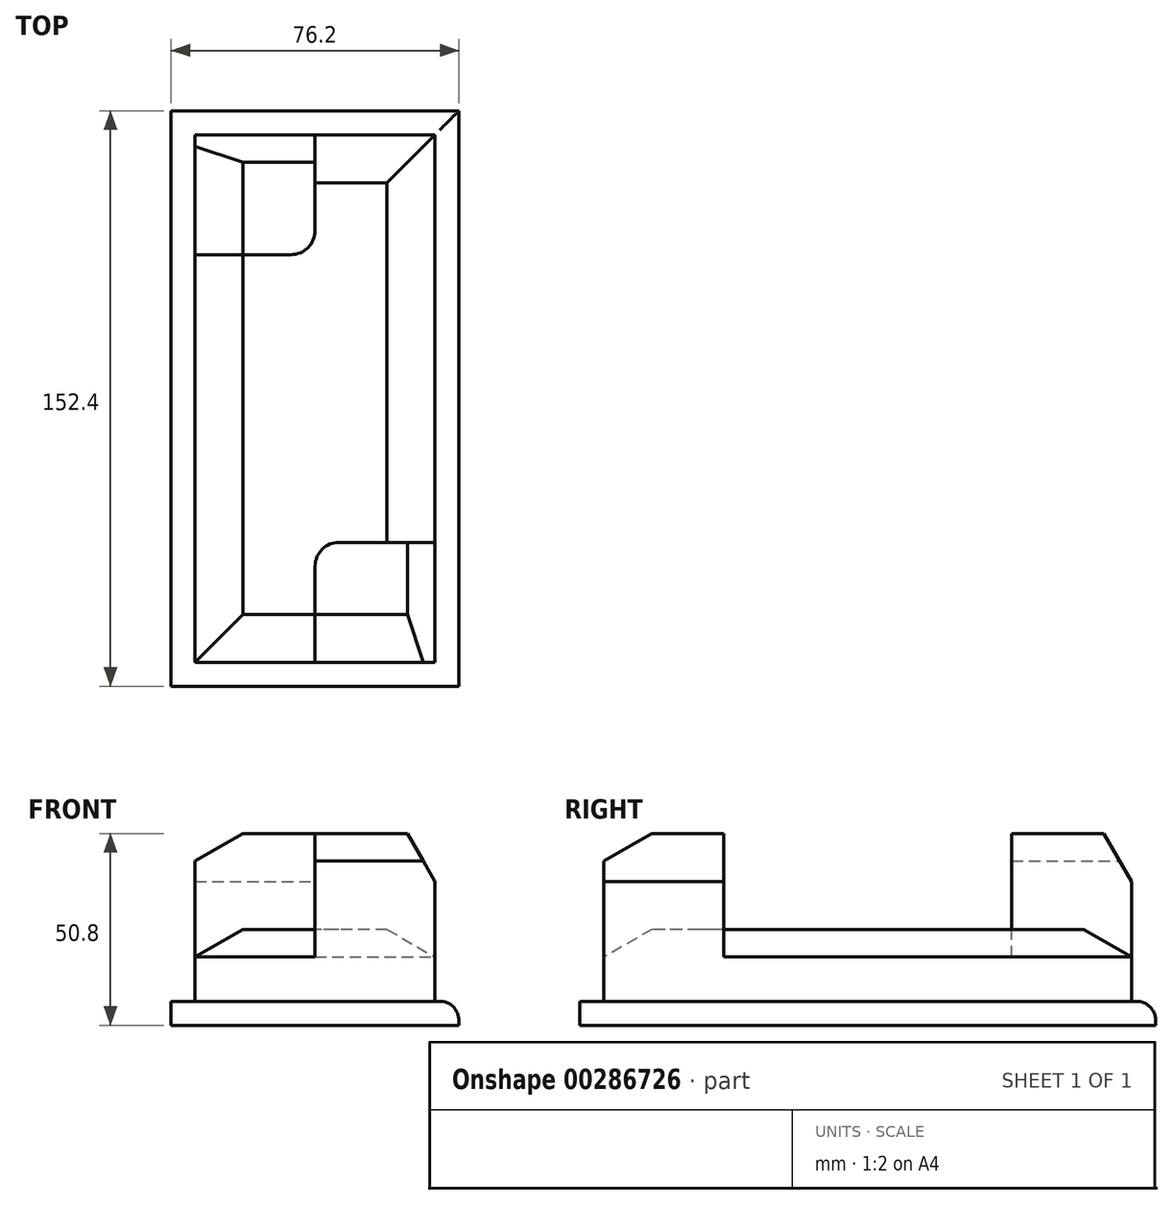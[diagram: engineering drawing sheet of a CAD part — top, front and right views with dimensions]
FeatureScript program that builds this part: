
annotation { "Feature Type Name" : "Feature", "Feature Type Description" : "" }
export const myFeature = defineFeature(function(context is Context, id is Id, definition is map)
    precondition{}
    {
        {
            var Q0;
            Q0=qCreatedBy(makeId("Top.planeOp"),FACE);
            var sketch = newSketch(context, id + "F0", { "sketchPlane" : qUnion([Q0])});
            skLineSegment(sketch, "E0.bottom", {"start": v(-35.8, 87.47) * mm, "end": v(40.4, 87.47) * mm});
            skLineSegment(sketch, "E0.top", {"start": v(-35.8, -64.93) * mm, "end": v(40.4, -64.93) * mm});
            skLineSegment(sketch, "E0.left", {"start": v(-35.8, 87.47) * mm, "end": v(-35.8, -64.93) * mm});
            skLineSegment(sketch, "E0.right", {"start": v(40.4, 87.47) * mm, "end": v(40.4, -64.93) * mm});
            skLineSegment(sketch, "E1.bottom", {"start": v(-29.45, 81.12) * mm, "end": v(34.05, 81.12) * mm});
            skLineSegment(sketch, "E1.top", {"start": v(-29.45, -58.58) * mm, "end": v(34.05, -58.58) * mm});
            skLineSegment(sketch, "E1.left", {"start": v(-29.45, 81.12) * mm, "end": v(-29.45, -58.58) * mm});
            skLineSegment(sketch, "E1.right", {"start": v(34.05, 81.12) * mm, "end": v(34.05, -58.58) * mm});
            skLineSegment(sketch, "E2", {"start": v(-29.45, 49.37) * mm, "end": v(2.3, 49.37) * mm});
            skLineSegment(sketch, "E3", {"start": v(2.3, 49.37) * mm, "end": v(2.3, 81.12) * mm});
            skPoint(sketch, "E3.endSnap0", {"position": v(2.3, 81.12) * mm});
            skLineSegment(sketch, "E4", {"start": v(34.05, -26.83) * mm, "end": v(2.3, -26.83) * mm});
            skLineSegment(sketch, "E5", {"start": v(2.3, -26.83) * mm, "end": v(2.3, -58.58) * mm});
            skSolve(sketch);
        }
        {
            var Q0;
            Q0=makeQuery(id+"F0.imprint","IMPRINT",FACE,{"disambiguationData":[TD([[makeQuery(id+"F0.imprint","IMPRINT",EDGE,{"derivedFrom":sQuery(id+"F0.wireOp",EDGE,"E0.bottom")}),-1.0]])]});
            extrude(context, id + "F1", {"entities" : qUnion([Q0]), "depth" : 6.35 * mm});
        }
        {
            var Q0;
            {var subQ3=sQuery(id+"F0.wireOp",EDGE,"E2");Q0=makeQuery(id+"F0.imprint","IMPRINT",FACE,{"disambiguationData":[TD([[makeQuery(id+"F0.imprint","IMPRINT",EDGE,{"derivedFrom":subQ3}),-1.0]])]});}
            extrude(context, id + "F2", {"entities" : qUnion([Q0]), "operationType" : NewBodyOperationType.ADD, "depth" : 25.4 * mm});
        }
        {
            var Q0;
            {var subQ4=sQuery(id+"F0.wireOp",EDGE,"E2");Q0=makeQuery(id+"F0.imprint","IMPRINT",FACE,{"disambiguationData":[TD([[makeQuery(id+"F0.imprint","IMPRINT",EDGE,{"derivedFrom":subQ4}),1.0]])]});}
            var Q1;
            {var subQ4=sQuery(id+"F0.wireOp",EDGE,"E4");Q1=makeQuery(id+"F0.imprint","IMPRINT",FACE,{"disambiguationData":[TD([[makeQuery(id+"F0.imprint","IMPRINT",EDGE,{"derivedFrom":subQ4}),1.0]])]});}
            extrude(context, id + "F3", {"entities" : qUnion([Q0, Q1]), "operationType" : NewBodyOperationType.ADD, "depth" : 50.8 * mm});
        }
        {
            var Q0;
            Q0=makeQuery(id+"F2.opExtrude","CAP_EDGE",EDGE,{"disambiguationData":[OSD([sQuery(id+"F0.wireOp",EDGE,"E1.left")])],"isStart":false});
            var Q1;
            Q1=makeQuery(id+"F2.opExtrude","CAP_EDGE",EDGE,{"disambiguationData":[OSD([sQuery(id+"F0.wireOp",EDGE,"E1.top")])],"isStart":false});
            var Q2;
            Q2=makeQuery(id+"F3.opExtrude","CAP_EDGE",EDGE,{"disambiguationData":[OSD([sQuery(id+"F0.wireOp",EDGE,"E1.top")])],"isStart":false});
            var Q3;
            Q3=makeQuery(id+"F3.opExtrude","CAP_EDGE",EDGE,{"disambiguationData":[OSD([sQuery(id+"F0.wireOp",EDGE,"E1.left")])],"isStart":false});
            var Q4;
            Q4=makeQuery(id+"F3.opExtrude","CAP_EDGE",EDGE,{"disambiguationData":[OSD([sQuery(id+"F0.wireOp",EDGE,"E1.right")])],"isStart":false});
            var Q5;
            Q5=makeQuery(id+"F2.opExtrude","CAP_EDGE",EDGE,{"disambiguationData":[OSD([sQuery(id+"F0.wireOp",EDGE,"E1.right")])],"isStart":false});
            var Q6;
            Q6=makeQuery(id+"F2.opExtrude","CAP_EDGE",EDGE,{"disambiguationData":[OSD([sQuery(id+"F0.wireOp",EDGE,"E1.bottom")])],"isStart":false});
            var Q7;
            Q7=makeQuery(id+"F3.opExtrude","CAP_EDGE",EDGE,{"disambiguationData":[OSD([sQuery(id+"F0.wireOp",EDGE,"E1.bottom")])],"isStart":false});
            chamfer(context, id + "F4", {"entities" : qUnion([Q0, Q1, Q2, Q3, Q4, Q5, Q6, Q7]), "chamferType" : ChamferType.OFFSET_ANGLE, "width" : 12.7 * mm, "oppositeDirection" : false, "angle" : 30 * degree, "tangentPropagation" : true});
        }
        {
            var Q0;
            Q0=makeQuery(id+"F3.opExtrude","SWEPT_EDGE",EDGE,{"disambiguationData":[OSD([sQuery(id+"F0.wireOp",EDGE,"E2"),sQuery(id+"F0.wireOp",EDGE,"E3")])]});
            var Q1;
            Q1=makeQuery(id+"F3.opExtrude","SWEPT_EDGE",EDGE,{"disambiguationData":[OSD([sQuery(id+"F0.wireOp",EDGE,"E4"),sQuery(id+"F0.wireOp",EDGE,"E5")])]});
            fillet(context, id + "F5", {"entities" : qUnion([Q0, Q1]), "radius" : 6.35 * mm, "tangentPropagation" : true, "allowEdgeOverflow" : false});
        }
        {
            var Q0;
            Q0=makeQuery(id+"F1.opExtrude","CAP_EDGE",EDGE,{"disambiguationData":[OSD([sQuery(id+"F0.wireOp",EDGE,"E0.bottom")])],"isStart":false});
            var Q1;
            Q1=makeQuery(id+"F1.opExtrude","CAP_EDGE",EDGE,{"disambiguationData":[OSD([sQuery(id+"F0.wireOp",EDGE,"E0.right")])],"isStart":false});
            fillet(context, id + "F6", {"entities" : qUnion([Q0, Q1]), "radius" : 5.08 * mm, "tangentPropagation" : true, "allowEdgeOverflow" : false});
        }
    });
